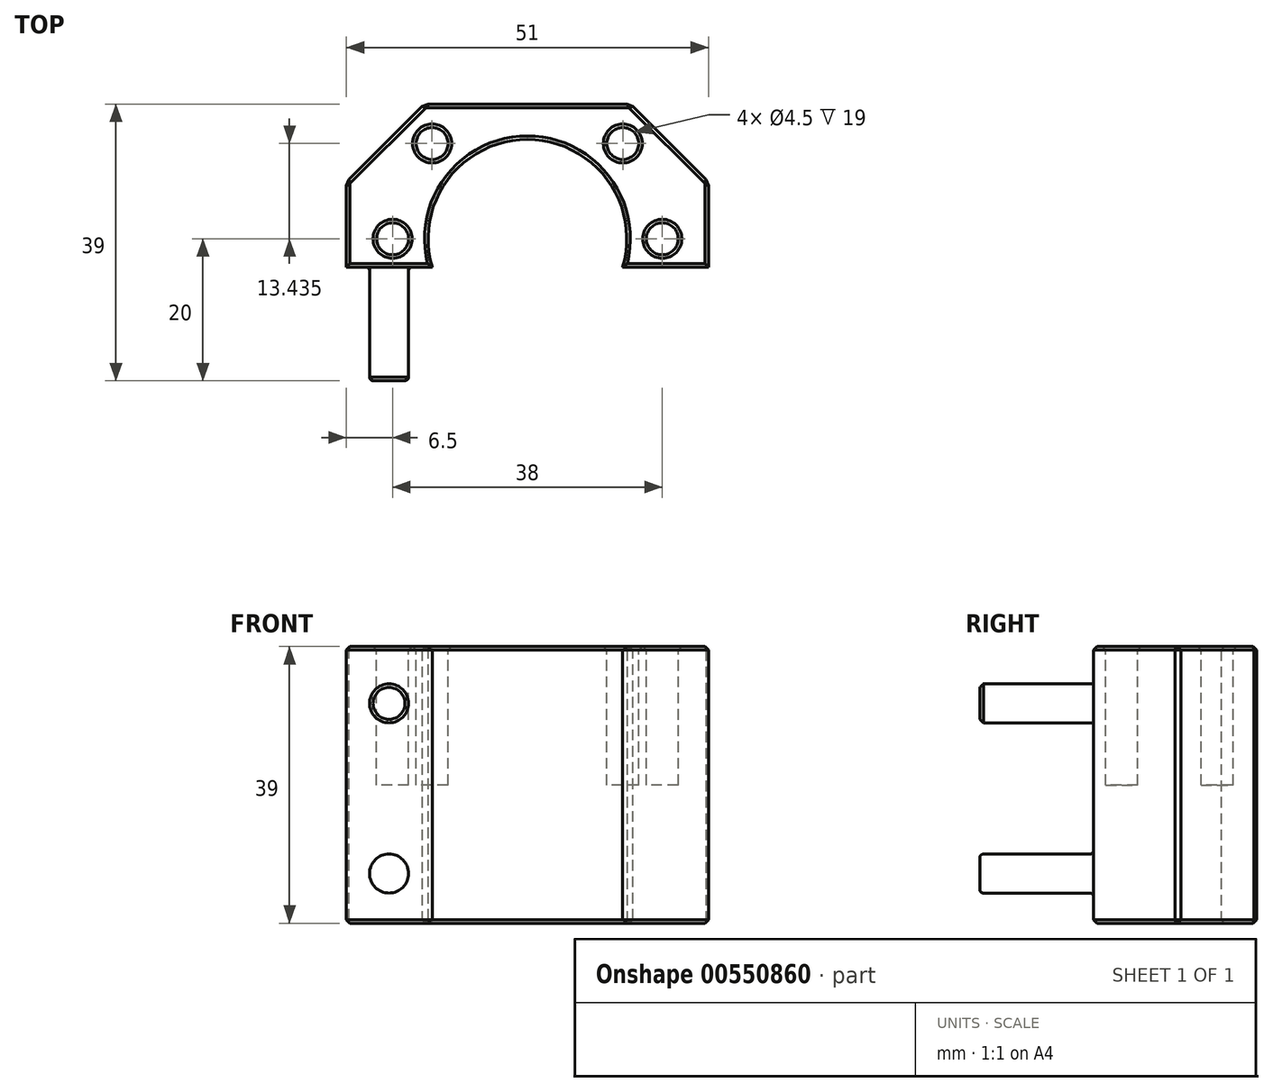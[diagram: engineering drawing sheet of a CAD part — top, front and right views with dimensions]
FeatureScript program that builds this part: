
annotation { "Feature Type Name" : "Feature", "Feature Type Description" : "" }
export const myFeature = defineFeature(function(context is Context, id is Id, definition is map)
    precondition{}
    {
        {
            var Q0;
            Q0=qCreatedBy(makeId("Top.planeOp"),FACE);
            var sketch = newSketch(context, id + "F0", { "sketchPlane" : qUnion([Q0])});
            skLineSegment(sketch, "E0", {"start": v(-25.5, -20) * mm, "end": v(25.5, -20) * mm});
            skLineSegment(sketch, "E1", {"start": v(25.5, 8) * mm, "end": v(14.5, 19) * mm});
            skLineSegment(sketch, "E2", {"start": v(14.5, 19) * mm, "end": v(-14.5, 19) * mm});
            skLineSegment(sketch, "E3", {"start": v(-14.5, 19) * mm, "end": v(-25.5, 8) * mm});
            skLineSegment(sketch, "E4", {"start": v(-25.5, 8) * mm, "end": v(-25.5, -20) * mm});
            skLineSegment(sketch, "E5", {"start": v(25.5, -20) * mm, "end": v(25.5, 8) * mm});
            skCircle(sketch, "E6", {"center": v(0, 0) * mm, "radius": 14 * mm});
            skSolve(sketch);
        }
        {
            var Q0;
            Q0 = qSketchRegion(id + "F0", true);
            extrude(context, id + "F1", {"entities" : qUnion([Q0]), "depth" : 19.5 * mm, "offsetDistance" : 25 * mm, "hasSecondDirection" : true, "secondDirectionOppositeDirection" : true, "secondDirectionDepth" : 19.5 * mm});
        }
        {
            var Q0;
            Q0=makeQuery(id+"F1.opExtrude","CAP_FACE",FACE,{"disambiguationData":[OSD([sQuery(id+"F0.wireOp",EDGE,"E0"),sQuery(id+"F0.wireOp",EDGE,"E1"),sQuery(id+"F0.wireOp",EDGE,"E2"),sQuery(id+"F0.wireOp",EDGE,"E3"),sQuery(id+"F0.wireOp",EDGE,"E4"),sQuery(id+"F0.wireOp",EDGE,"E5"),sQuery(id+"F0.wireOp",EDGE,"E6")])],"isStart":false});
            var sketch = newSketch(context, id + "F2", { "sketchPlane" : qUnion([Q0])});
            skCircle(sketch, "E7", {"center": v(0, 0) * mm, "radius": 19 * mm, "construction": true});
            skPoint(sketch, "E8", {"position": v(19, 0) * mm});
            skPoint(sketch, "E9", {"position": v(13.44, 13.44) * mm});
            skPoint(sketch, "E10", {"position": v(13.44, -13.44) * mm});
            skCircle(sketch, "E11", {"center": v(19, 0) * mm, "radius": 2.25 * mm});
            skCircle(sketch, "E12", {"center": v(13.44, 13.44) * mm, "radius": 2.25 * mm});
            skCircle(sketch, "E13", {"center": v(13.44, -13.44) * mm, "radius": 2.25 * mm});
            skCircle(sketch, "E14.MirrorC", {"center": v(-13.44, 13.44) * mm, "radius": 2.25 * mm});
            skCircle(sketch, "E15.MirrorC", {"center": v(-19, 0) * mm, "radius": 2.25 * mm});
            skCircle(sketch, "E16.MirrorC", {"center": v(-13.44, -13.44) * mm, "radius": 2.25 * mm});
            skLineSegment(sketch, "E17", {"start": v(0, 0) * mm, "end": v(13.44, 13.44) * mm, "construction": true});
            skLineSegment(sketch, "E18", {"start": v(0, 0) * mm, "end": v(19, 0) * mm, "construction": true});
            skLineSegment(sketch, "E19", {"start": v(0, 0) * mm, "end": v(13.44, -13.44) * mm, "construction": true});
            skSolve(sketch);
        }
        {
            var Q0;
            Q0 = qSketchRegion(id + "F2", true);
            extrude(context, id + "F3", {"entities" : qUnion([Q0]), "operationType" : NewBodyOperationType.REMOVE, "oppositeDirection" : true, "depth" : 19.5 * mm, "offsetDistance" : 25 * mm});
        }
        {
            var Q0;
            Q0=makeQuery(id+"F1.opExtrude","SWEPT_FACE",FACE,{"disambiguationData":[OSD([sQuery(id+"F0.wireOp",EDGE,"E0")])]});
            var sketch = newSketch(context, id + "F4", { "sketchPlane" : qUnion([Q0])});
            skCircle(sketch, "E20", {"center": v(19.5, 11.5) * mm, "radius": 2.75 * mm});
            skCircle(sketch, "E21", {"center": v(19.5, -12.5) * mm, "radius": 2.75 * mm});
            skCircle(sketch, "E22.MirrorC", {"center": v(-19.5, 11.5) * mm, "radius": 2.75 * mm});
            skCircle(sketch, "E23.MirrorC", {"center": v(-19.5, -12.5) * mm, "radius": 2.75 * mm});
            skSolve(sketch);
        }
        {
            var Q0;
            Q0=makeQuery(id+"F4.imprint","IMPRINT",FACE,{"disambiguationData":[TD([[makeQuery(id+"F4.imprint","IMPRINT",EDGE,{"derivedFrom":sQuery(id+"F4.wireOp",EDGE,"E22.MirrorC")}),-1.0]])]});
            var Q1;
            Q1=makeQuery(id+"F4.imprint","IMPRINT",FACE,{"disambiguationData":[TD([[makeQuery(id+"F4.imprint","IMPRINT",EDGE,{"derivedFrom":sQuery(id+"F4.wireOp",EDGE,"E20")}),1.0]])]});
            var Q2;
            Q2=makeQuery(id+"F4.imprint","IMPRINT",FACE,{"disambiguationData":[TD([[makeQuery(id+"F4.imprint","IMPRINT",EDGE,{"derivedFrom":sQuery(id+"F4.wireOp",EDGE,"E23.MirrorC")}),-1.0]])]});
            var Q3;
            Q3=makeQuery(id+"F4.imprint","IMPRINT",FACE,{"disambiguationData":[TD([[makeQuery(id+"F4.imprint","IMPRINT",EDGE,{"derivedFrom":sQuery(id+"F4.wireOp",EDGE,"E21")}),1.0]])]});
            extrude(context, id + "F5", {"entities" : qUnion([Q0, Q1, Q2, Q3]), "operationType" : NewBodyOperationType.REMOVE, "oppositeDirection" : true, "depth" : 16 * mm, "offsetDistance" : 25 * mm});
        }
        {
            var Q0;
            Q0=makeQuery(id+"F3.boolean.opBoolean","COPY",EDGE,{"derivedFrom":makeQuery(id+"F3.opExtrude","CAP_EDGE",EDGE,{"disambiguationData":[OSD([sQuery(id+"F2.wireOp",EDGE,"E15.MirrorC")])],"isStart":true})});
            var Q1;
            Q1=makeQuery(id+"F3.boolean.opBoolean","COPY",EDGE,{"derivedFrom":makeQuery(id+"F3.opExtrude","CAP_EDGE",EDGE,{"disambiguationData":[OSD([sQuery(id+"F2.wireOp",EDGE,"E14.MirrorC")])],"isStart":true})});
            var Q2;
            Q2=makeQuery(id+"F3.boolean.opBoolean","COPY",EDGE,{"derivedFrom":makeQuery(id+"F3.opExtrude","CAP_EDGE",EDGE,{"disambiguationData":[OSD([sQuery(id+"F2.wireOp",EDGE,"E12")])],"isStart":true})});
            var Q3;
            Q3=makeQuery(id+"F3.boolean.opBoolean","COPY",EDGE,{"derivedFrom":makeQuery(id+"F3.opExtrude","CAP_EDGE",EDGE,{"disambiguationData":[OSD([sQuery(id+"F2.wireOp",EDGE,"E11")])],"isStart":true})});
            var Q4;
            Q4=makeQuery(id+"F3.boolean.opBoolean","COPY",EDGE,{"derivedFrom":makeQuery(id+"F3.opExtrude","CAP_EDGE",EDGE,{"disambiguationData":[OSD([sQuery(id+"F2.wireOp",EDGE,"E13")])],"isStart":true})});
            var Q5;
            Q5=makeQuery(id+"F3.boolean.opBoolean","COPY",EDGE,{"derivedFrom":makeQuery(id+"F3.opExtrude","CAP_EDGE",EDGE,{"disambiguationData":[OSD([sQuery(id+"F2.wireOp",EDGE,"E16.MirrorC")])],"isStart":true})});
            var Q6;
            Q6=makeQuery(id+"F5.boolean.opBoolean","COPY",EDGE,{"derivedFrom":makeQuery(id+"F5.opExtrude","CAP_EDGE",EDGE,{"disambiguationData":[OSD([sQuery(id+"F4.wireOp",EDGE,"E20")])],"isStart":true})});
            var Q7;
            Q7=makeQuery(id+"F5.boolean.opBoolean","COPY",EDGE,{"derivedFrom":makeQuery(id+"F5.opExtrude","CAP_EDGE",EDGE,{"disambiguationData":[OSD([sQuery(id+"F4.wireOp",EDGE,"E21")])],"isStart":true})});
            var Q8;
            Q8=makeQuery(id+"F5.boolean.opBoolean","COPY",FACE,{"derivedFrom":makeQuery(id+"F5.opExtrude","SWEPT_FACE",FACE,{"disambiguationData":[OSD([sQuery(id+"F4.wireOp",EDGE,"E23.MirrorC")])]})});
            var Q9;
            Q9=makeQuery(id+"F5.boolean.opBoolean","COPY",EDGE,{"derivedFrom":makeQuery(id+"F5.opExtrude","CAP_EDGE",EDGE,{"disambiguationData":[OSD([sQuery(id+"F4.wireOp",EDGE,"E22.MirrorC")])],"isStart":true})});
            fillet(context, id + "F6", {"entities" : qUnion([Q0, Q1, Q2, Q3, Q4, Q5, Q6, Q7, Q8, Q9]), "radius" : .5 * mm, "tangentPropagation" : true, "allowEdgeOverflow" : false});
        }
        {
            var Q0;
            Q0=makeQuery(id+"F1.opExtrude","CAP_FACE",FACE,{"disambiguationData":[OSD([sQuery(id+"F0.wireOp",EDGE,"E0"),sQuery(id+"F0.wireOp",EDGE,"E1"),sQuery(id+"F0.wireOp",EDGE,"E2"),sQuery(id+"F0.wireOp",EDGE,"E3"),sQuery(id+"F0.wireOp",EDGE,"E4"),sQuery(id+"F0.wireOp",EDGE,"E5"),sQuery(id+"F0.wireOp",EDGE,"E6")])],"isStart":false});
            var Q1;
            Q1=makeQuery(id+"F1.opExtrude","SWEPT_FACE",FACE,{"disambiguationData":[OSD([sQuery(id+"F0.wireOp",EDGE,"E3")])]});
            var Q2;
            Q2=makeQuery(id+"F1.opExtrude","SWEPT_FACE",FACE,{"disambiguationData":[OSD([sQuery(id+"F0.wireOp",EDGE,"E2")])]});
            var Q3;
            Q3=makeQuery(id+"F1.opExtrude","SWEPT_FACE",FACE,{"disambiguationData":[OSD([sQuery(id+"F0.wireOp",EDGE,"E1")])]});
            var Q4;
            Q4=makeQuery(id+"F1.opExtrude","CAP_FACE",FACE,{"disambiguationData":[OSD([sQuery(id+"F0.wireOp",EDGE,"E0"),sQuery(id+"F0.wireOp",EDGE,"E1"),sQuery(id+"F0.wireOp",EDGE,"E2"),sQuery(id+"F0.wireOp",EDGE,"E3"),sQuery(id+"F0.wireOp",EDGE,"E4"),sQuery(id+"F0.wireOp",EDGE,"E5"),sQuery(id+"F0.wireOp",EDGE,"E6")])],"isStart":true});
            var Q5;
            Q5=makeQuery(id+"F1.opExtrude","SWEPT_FACE",FACE,{"disambiguationData":[OSD([sQuery(id+"F0.wireOp",EDGE,"E0")])]});
            chamfer(context, id + "F7", {"entities" : qUnion([Q0, Q1, Q2, Q3, Q4, Q5]), "width" : .5 * mm, "tangentPropagation" : true});
        }
    });
